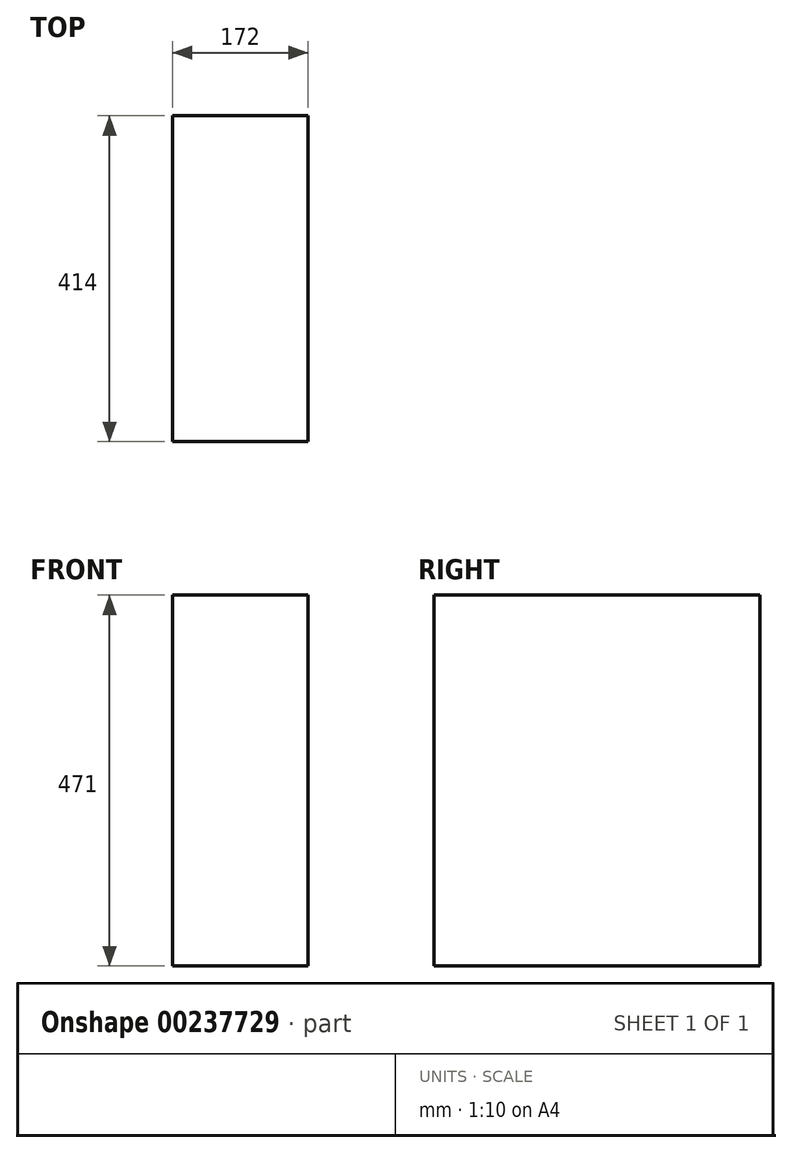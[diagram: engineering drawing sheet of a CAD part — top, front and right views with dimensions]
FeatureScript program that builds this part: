
annotation { "Feature Type Name" : "Feature", "Feature Type Description" : "" }
export const myFeature = defineFeature(function(context is Context, id is Id, definition is map)
    precondition{}
    {
        {
            var Q0;
            Q0=qCreatedBy(makeId("Top.planeOp"),FACE);
            var sketch = newSketch(context, id + "F0", { "sketchPlane" : qUnion([Q0])});
            skLineSegment(sketch, "E0.bottom", {"start": v(0, 0) * mm, "end": v(172, 0) * mm});
            skLineSegment(sketch, "E0.top", {"start": v(0, 414) * mm, "end": v(172, 414) * mm});
            skLineSegment(sketch, "E0.left", {"start": v(0, 0) * mm, "end": v(0, 414) * mm});
            skLineSegment(sketch, "E0.right", {"start": v(172, 0) * mm, "end": v(172, 414) * mm});
            skSolve(sketch);
        }
        {
            var Q0;
            Q0 = qSketchRegion(id + "F0", true);
            extrude(context, id + "F1", {"entities" : qUnion([Q0]), "depth" : 471 * mm});
        }
    });
